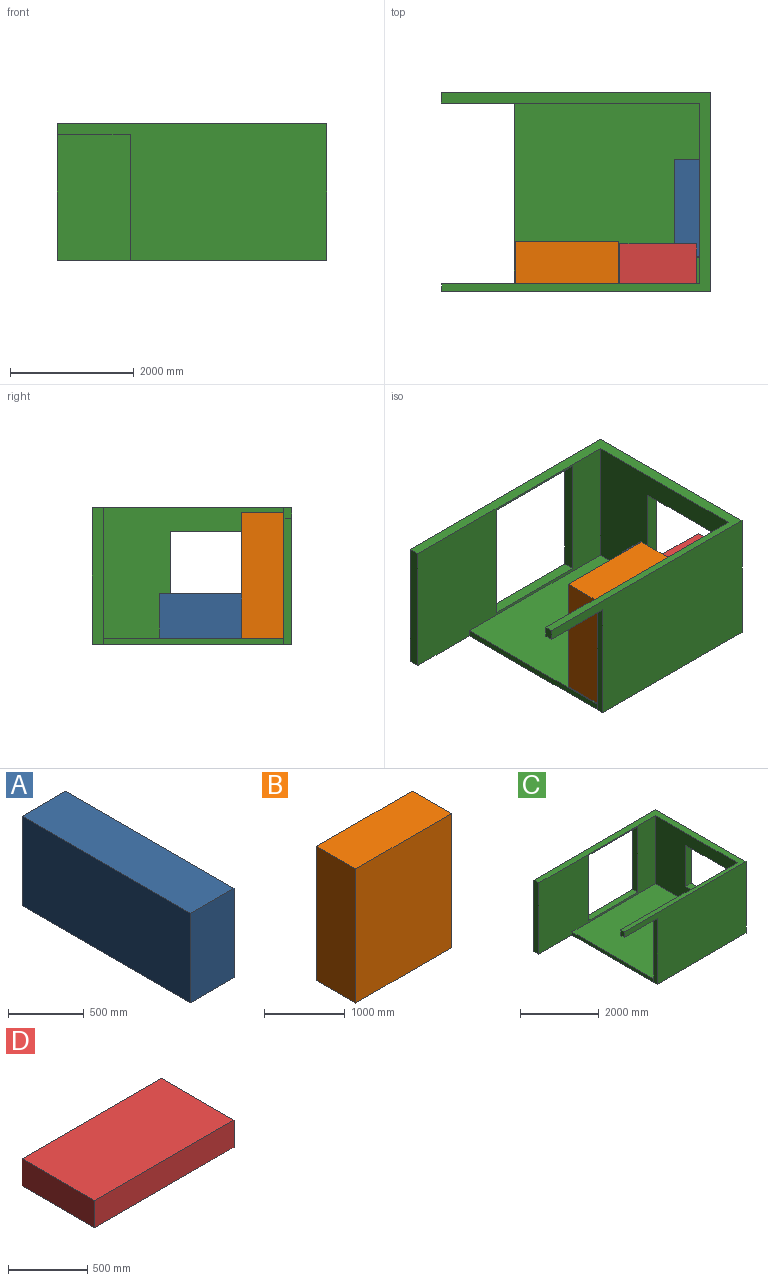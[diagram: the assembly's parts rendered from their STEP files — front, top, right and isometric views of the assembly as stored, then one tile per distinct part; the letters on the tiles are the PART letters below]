
ASSEMBLY  parts=4 mates=5
PART A: 6 faces, bbox 406.4x1574.8x723.9 mm
  f0: plane 723.9x406.4mm, normal (0,1,0), area 294193mm2, adj f1,f3,f4,f5
  f1: plane 1574.8x723.9mm, normal (-1,0,0), area 1139997.7mm2, adj f0,f2,f4,f5
  f2: plane 723.9x406.4mm, normal (0,-1,0), area 294193mm2, adj f1,f3,f4,f5
  f3: plane 1574.8x723.9mm, normal (1,0,0), area 1139997.7mm2, adj f0,f2,f4,f5
  f4: plane 1574.8x406.4mm, normal (0,0,1), area 639998.7mm2, adj f0,f1,f2,f3
  f5: plane 1574.8x406.4mm, normal (0,0,-1), area 639998.7mm2, adj f0,f1,f2,f3
PART B: 6 faces, bbox 1676.4x685.8x2032 mm
  f0: plane 2032x1676.4mm, normal (0,1,0), area 3406444.8mm2, adj f1,f3,f4,f5
  f1: plane 2032x685.8mm, normal (-1,0,0), area 1393545.6mm2, adj f0,f2,f4,f5
  f2: plane 2032x1676.4mm, normal (0,-1,0), area 3406444.8mm2, adj f1,f3,f4,f5
  f3: plane 2032x685.8mm, normal (1,0,0), area 1393545.6mm2, adj f0,f2,f4,f5
  f4: plane 1676.4x685.8mm, normal (0,0,1), area 1149675.1mm2, adj f0,f1,f2,f3
  f5: plane 1676.4x685.8mm, normal (0,0,-1), area 1149675.1mm2, adj f0,f1,f2,f3
PART C: 22 faces, bbox 4371.7x3232.2x2216.2 mm
  f0: plane 2927.37x101.62mm, normal (-1,0,0), area 297418.8mm2, adj f1,f2,f14,f17
  f1: plane 2997.2x2927.35mm, normal (0,0,1), area 8773853.4mm2, adj f0,f5,f10,f17
  f2: plane 4371.67x3232.15mm, normal (0,0,-1), area 10513635.2mm2, adj f0,f4,f12,f14,f15,f16,f17
  f3: plane 4371.67x3232.15mm, normal (0,0,1), area 1889037.7mm2, adj f4,f5,f10,f11,f12,f15,f16,f17
  f4: plane 3232.15x2216.15mm, normal (1,0,0), area 4942207.9mm2, adj f2,f3,f6,f7,f8,f9,f12,f16
  f5: plane 2927.35x2114.55mm, normal (-1,0,0), area 3969306.6mm2, adj f1,f3,f6,f7,f8,f9,f10,f17
  f6: plane 1276.35x190.5mm, normal (0,1,0), area 243144.7mm2, adj f4,f5,f7,f9
  f7: plane 1739.9x190.5mm, normal (0,0,-1), area 331451mm2, adj f4,f5,f6,f8
  f8: plane 1276.35x190.5mm, normal (0,-1,0), area 243144.7mm2, adj f4,f5,f7,f9
  f9: plane 1739.9x190.5mm, normal (0,0,1), area 331451mm2, adj f4,f5,f6,f8
  f10: plane 4172.45x2114.55mm, normal (0,1,0), area 6542974.1mm2, adj f1,f3,f5,f11,f13,f14
  f11: plane 174.63x127mm, normal (-1,0,0), area 22177.4mm2, adj f3,f10,f12,f13
  f12: plane 4362.95x2216.15mm, normal (0,-1,0), area 7269667mm2, adj f2,f3,f4,f11,f13,f14
  f13: plane 1175.24x127mm, normal (0,0,-1), area 149255.9mm2, adj f10,f11,f12,f14
  f14: plane 2041.54x127.02mm, normal (-1,0,0), area 259273.7mm2, adj f0,f2,f10,f12,f13
  f15: plane 2216.15x177.8mm, normal (-1,0,0), area 394031.5mm2, adj f2,f3,f16,f17
  f16: plane 4371.67x2216.15mm, normal (0,1,0), area 6126989.6mm2, adj f2,f3,f4,f15,f18,f19,f20,f21
  f17: plane 4181.17x2216.15mm, normal (0,-1,0), area 5400297.5mm2, adj f0,f1,f2,f3,f5,f15,f18,f19
  f18: plane 2032x177.8mm, normal (-1,0,0), area 361289.6mm2, adj f16,f17,f19,f21
  f19: plane 1752.6x177.8mm, normal (0,0,-1), area 311612.3mm2, adj f16,f17,f18,f20
  f20: plane 2032x177.8mm, normal (1,0,0), area 361289.6mm2, adj f16,f17,f19,f21
  f21: plane 1752.6x177.8mm, normal (0,0,1), area 311612.3mm2, adj f16,f17,f18,f20
PART D: 6 faces, bbox 1244.6x647.7x209.6 mm
  f0: plane 647.7x209.55mm, normal (1,0,0), area 135725.5mm2, adj f1,f3,f4,f5
  f1: plane 1244.6x647.7mm, normal (0,0,-1), area 806127.4mm2, adj f0,f2,f4,f5
  f2: plane 647.7x209.55mm, normal (-1,0,0), area 135725.5mm2, adj f1,f3,f4,f5
  f3: plane 1244.6x647.7mm, normal (0,0,1), area 806127.4mm2, adj f0,f2,f4,f5
  f4: plane 1244.6x209.55mm, normal (0,1,0), area 260805.9mm2, adj f0,f1,f2,f3
  f5: plane 1244.6x209.55mm, normal (0,-1,0), area 260805.9mm2, adj f0,f1,f2,f3
PLACE A t=(-63.02,194.44,0)mm
PLACE B t=(-211.67,-232.09,54.64)mm
PLACE C t=(0,0,-46.96)mm fixed
PLACE D t=(2.24,0,292.41)mm
MATE planar B.f2 <-> C.f10  axis (0,-1,0) through (-356.49,-1457.09,1070.64)mm
MATE planar D.f5 <-> C.f10  axis (0,-1,0) through (1119.16,-1457.09,1537.48)mm
MATE planar B.f5 <-> C.f1  axis (0,0,-1) through (-356.49,-1114.19,54.64)mm
MATE planar C.f5 <-> A.f3  axis (-1,0,0) through (1781.23,281.92,1090.6)mm
MATE planar A.f5 <-> C.f1  axis (0,0,-1) through (1578.03,-231.68,54.64)mm
